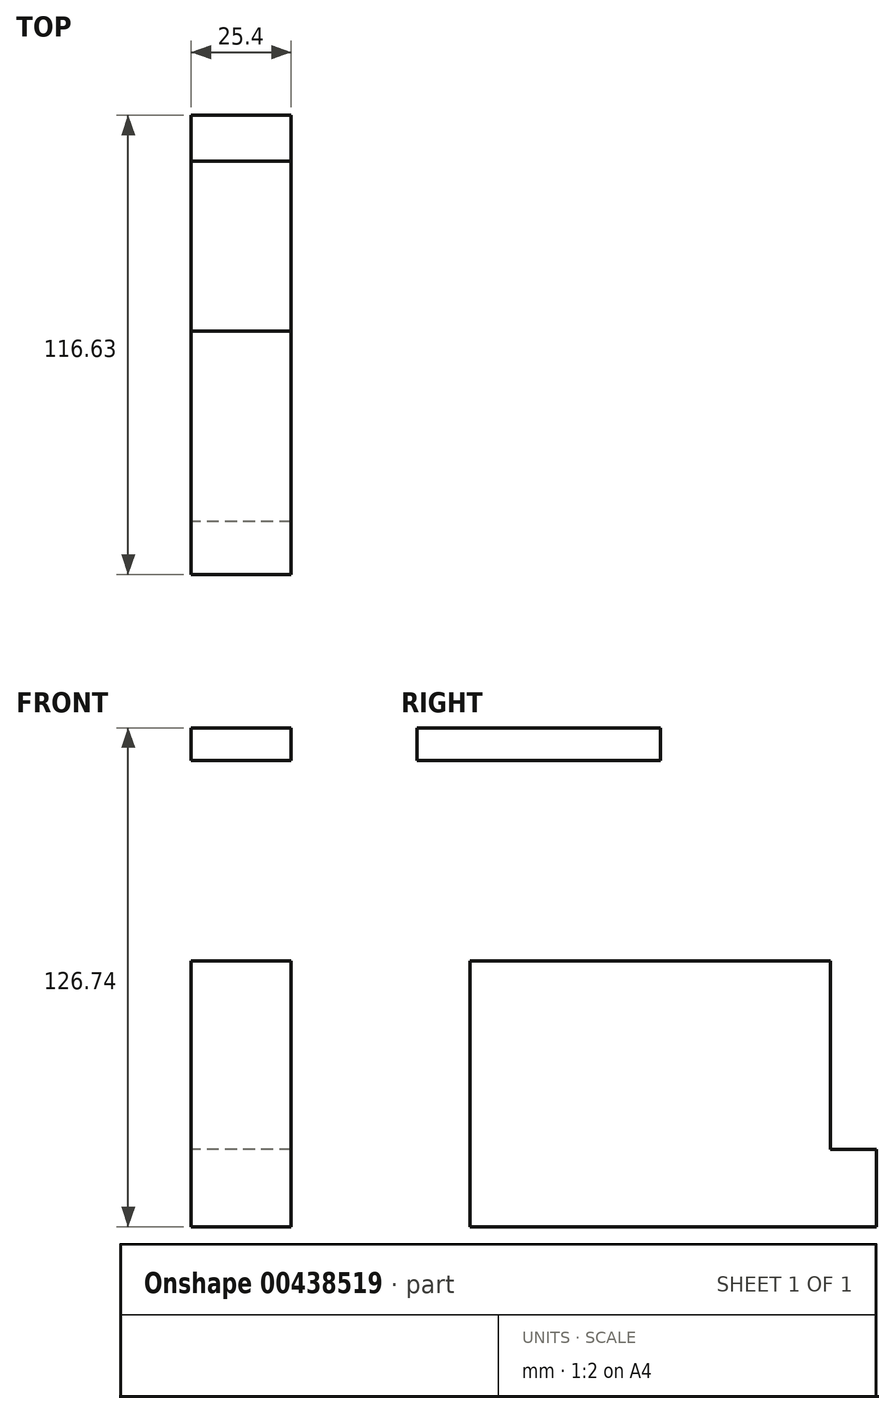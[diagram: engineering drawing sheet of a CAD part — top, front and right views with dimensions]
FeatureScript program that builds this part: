
annotation { "Feature Type Name" : "Feature", "Feature Type Description" : "" }
export const myFeature = defineFeature(function(context is Context, id is Id, definition is map)
    precondition{}
    {
        {
            var Q0;
            Q0=qCreatedBy(makeId("Right.planeOp"),FACE);
            var sketch = newSketch(context, id + "F0", { "sketchPlane" : qUnion([Q0])});
            skLineSegment(sketch, "E0.bottom", {"start": v(53.75, -33.96) * mm, "end": v(30.55, -33.96) * mm});
            skLineSegment(sketch, "E0.top", {"start": v(53.75, -14.3) * mm, "end": v(30.55, -14.3) * mm});
            skLineSegment(sketch, "E0.left", {"start": v(53.75, -33.96) * mm, "end": v(53.75, -14.3) * mm});
            skLineSegment(sketch, "E0.right", {"start": v(30.55, -33.96) * mm, "end": v(30.55, -14.3) * mm});
            skLineSegment(sketch, "E1.bottom", {"start": v(-62.88, 84.52) * mm, "end": v(-1.03, 84.52) * mm});
            skLineSegment(sketch, "E1.top", {"start": v(-62.88, 92.78) * mm, "end": v(-1.03, 92.78) * mm});
            skLineSegment(sketch, "E1.left", {"start": v(-62.88, 84.52) * mm, "end": v(-62.88, 92.78) * mm});
            skLineSegment(sketch, "E1.right", {"start": v(-1.03, 84.52) * mm, "end": v(-1.03, 92.78) * mm});
            skLineSegment(sketch, "E2.bottom", {"start": v(42.15, -33.96) * mm, "end": v(-49.5, -33.96) * mm});
            skLineSegment(sketch, "E2.top", {"start": v(42.15, 33.53) * mm, "end": v(-49.5, 33.53) * mm});
            skLineSegment(sketch, "E2.left", {"start": v(42.15, -33.96) * mm, "end": v(42.15, 33.53) * mm});
            skLineSegment(sketch, "E2.right", {"start": v(-49.5, -33.96) * mm, "end": v(-49.5, 33.53) * mm});
            skSolve(sketch);
        }
        {
            var Q0;
            Q0 = qSketchRegion(id + "F0", true);
            var Q1;
            {var subQ0=sQuery(id+"F0.wireOp",EDGE,"E0.right");Q1=makeQuery(id+"F0.imprint","IMPRINT",FACE,{"disambiguationData":[TD([[makeQuery(id+"F0.imprint","IMPRINT",EDGE,{"derivedFrom":subQ0}),-1.0]])]});}
            var Q2;
            {var subQ2=sQuery(id+"F0.wireOp",EDGE,"E0.right");Q2=makeQuery(id+"F0.imprint","IMPRINT",FACE,{"disambiguationData":[TD([[makeQuery(id+"F0.imprint","IMPRINT",EDGE,{"derivedFrom":subQ2}),1.0]])]});}
            extrude(context, id + "F1", {"entities" : qUnion([Q0, Q1, Q2]), "depth" : 25.4 * mm});
        }
    });
